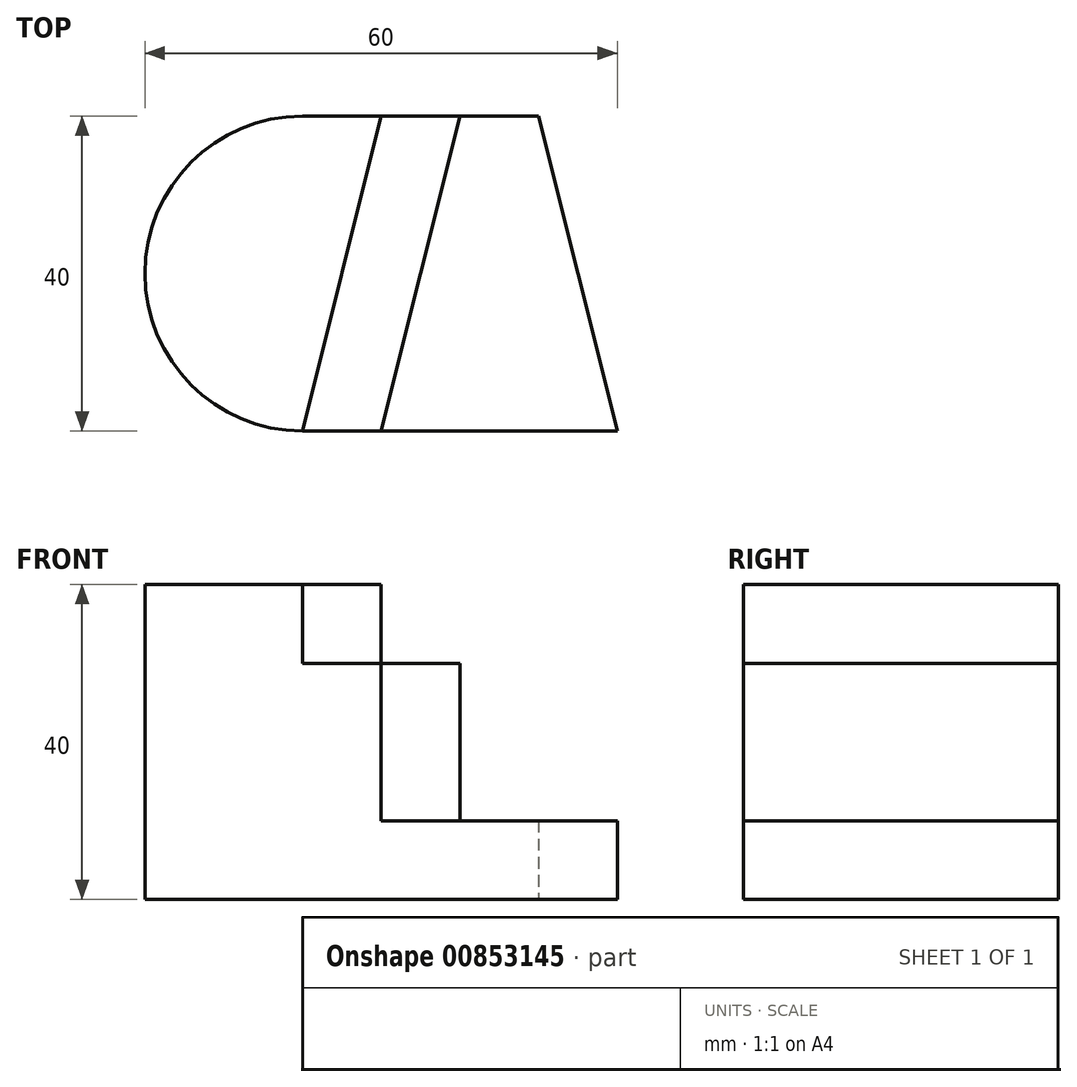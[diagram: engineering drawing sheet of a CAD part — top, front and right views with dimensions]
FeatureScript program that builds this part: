
annotation { "Feature Type Name" : "Feature", "Feature Type Description" : "" }
export const myFeature = defineFeature(function(context is Context, id is Id, definition is map)
    precondition{}
    {
        {
            var Q0;
            Q0=qCreatedBy(makeId("Top.planeOp"),FACE);
            var sketch = newSketch(context, id + "F0", { "sketchPlane" : qUnion([Q0])});
            skLineSegment(sketch, "E0", {"start": v(29.87, 0) * mm, "end": v(-10.13, 0) * mm});
            skLineSegment(sketch, "E1", {"start": v(-10.13, 40) * mm, "end": v(19.87, 40) * mm});
            skLineSegment(sketch, "E2", {"start": v(19.87, 40) * mm, "end": v(29.87, 0) * mm});
            skArc(sketch, "E3", {"start": v(-10.13, 40) * mm, "mid": v(-30.13, 20) * mm, "end": v(-10.13, 0) * mm});
            skSolve(sketch);
        }
        {
            var Q0;
            Q0 = qSketchRegion(id + "F0", true);
            extrude(context, id + "F1", {"entities" : qUnion([Q0]), "depth" : 40 * mm, "offsetDistance" : 25 * mm});
        }
        {
            var Q0;
            Q0=makeQuery(id+"F1.opExtrude","CAP_FACE",FACE,{"disambiguationData":[OSD([sQuery(id+"F0.wireOp",EDGE,"E0"),sQuery(id+"F0.wireOp",EDGE,"E1"),sQuery(id+"F0.wireOp",EDGE,"E2"),sQuery(id+"F0.wireOp",EDGE,"E3")])],"isStart":false});
            var sketch = newSketch(context, id + "F2", { "sketchPlane" : qUnion([Q0])});
            skLineSegment(sketch, "E4", {"start": v(9.87, 40) * mm, "end": v(-0.13, 0) * mm});
            skSolve(sketch);
        }
        {
            var Q0;
            Q0 = qSketchRegion(id + "F2", true);
            var Q1;
            {var subQ0=sQuery(id+"F2.wireOp",EDGE,"E4");Q1=makeQuery(id+"F2.imprint","IMPRINT",FACE,{"disambiguationData":[TD([[makeQuery(id+"F2.imprint","IMPRINT",EDGE,{"derivedFrom":subQ0}),1.0]])]});}
            extrude(context, id + "F3", {"entities" : qUnion([Q0, Q1]), "operationType" : NewBodyOperationType.REMOVE, "oppositeDirection" : true, "depth" : 30 * mm, "offsetDistance" : 25 * mm});
        }
        {
            var Q0;
            Q0=makeQuery(id+"F1.opExtrude","CAP_FACE",FACE,{"disambiguationData":[OSD([sQuery(id+"F0.wireOp",EDGE,"E0"),sQuery(id+"F0.wireOp",EDGE,"E1"),sQuery(id+"F0.wireOp",EDGE,"E2"),sQuery(id+"F0.wireOp",EDGE,"E3")])],"isStart":false});
            var sketch = newSketch(context, id + "F4", { "sketchPlane" : qUnion([Q0])});
            skLineSegment(sketch, "E5", {"start": v(-0.13, 40) * mm, "end": v(-10.13, 0) * mm});
            skSolve(sketch);
        }
        {
            var Q0;
            Q0 = qSketchRegion(id + "F4", true);
            var Q1;
            {var subQ0=sQuery(id+"F4.wireOp",EDGE,"E5");Q1=makeQuery(id+"F4.imprint","IMPRINT",FACE,{"disambiguationData":[TD([[makeQuery(id+"F4.imprint","IMPRINT",EDGE,{"derivedFrom":subQ0}),1.0]])]});}
            extrude(context, id + "F5", {"entities" : qUnion([Q0, Q1]), "operationType" : NewBodyOperationType.REMOVE, "oppositeDirection" : true, "depth" : 10 * mm, "offsetDistance" : 25 * mm});
        }
    });
